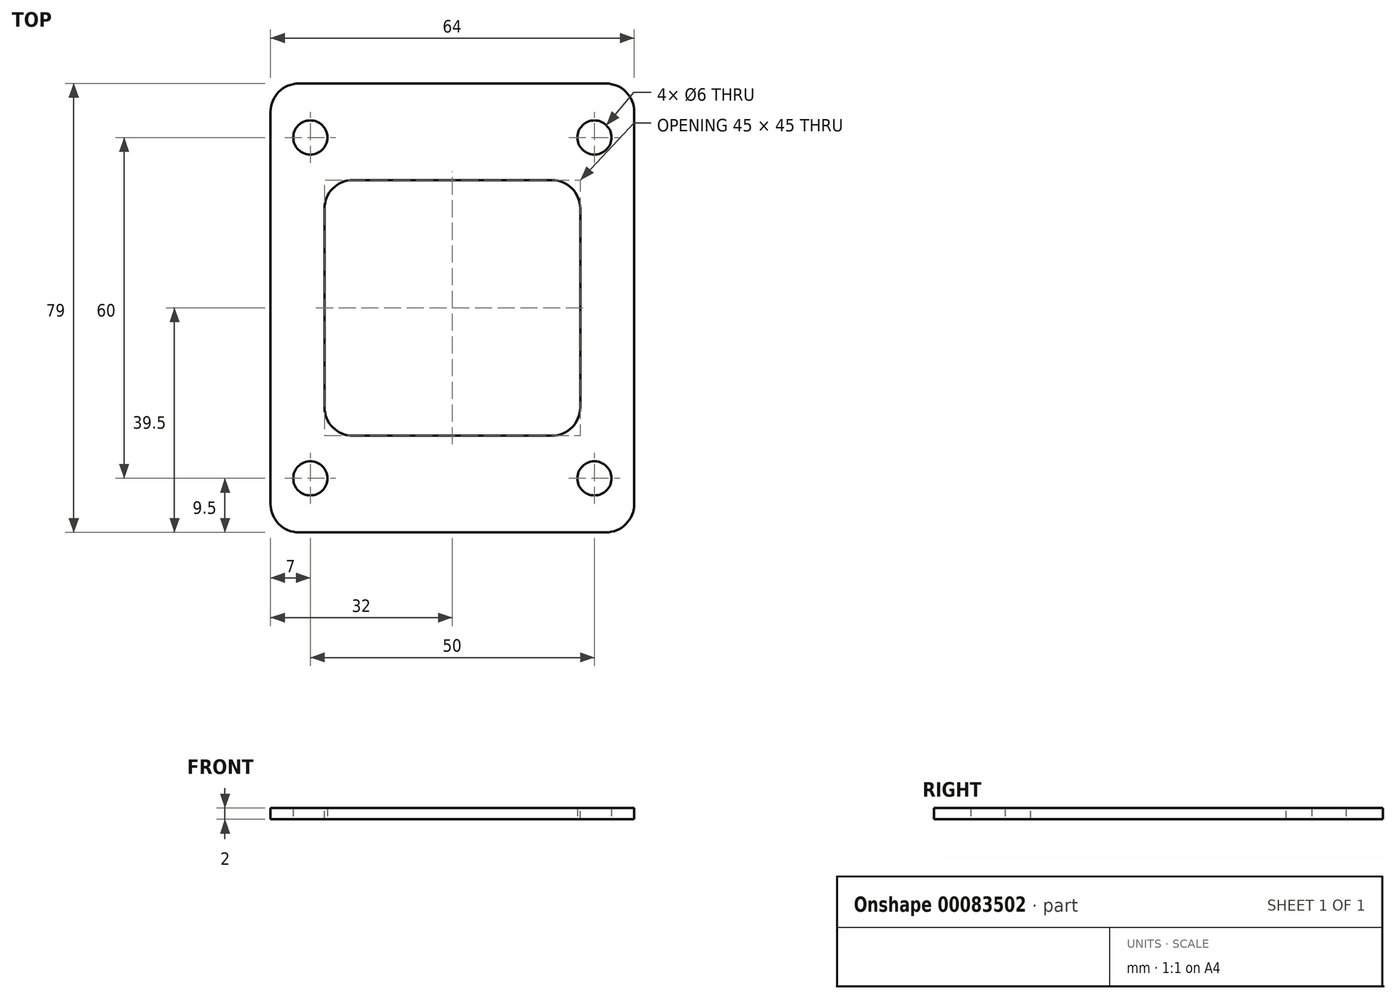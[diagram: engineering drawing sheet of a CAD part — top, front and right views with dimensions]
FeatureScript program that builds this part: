
annotation { "Feature Type Name" : "Feature", "Feature Type Description" : "" }
export const myFeature = defineFeature(function(context is Context, id is Id, definition is map)
    precondition{}
    {
        {
            var Q0;
            Q0=qCreatedBy(makeId("Top.planeOp"),FACE);
            var sketch = newSketch(context, id + "F0", { "sketchPlane" : qUnion([Q0])});
            skLineSegment(sketch, "E0.bottom", {"start": v(32, -39.5) * mm, "end": v(-32, -39.5) * mm});
            skLineSegment(sketch, "E0.top", {"start": v(32, 39.5) * mm, "end": v(-32, 39.5) * mm});
            skLineSegment(sketch, "E0.left", {"start": v(32, -39.5) * mm, "end": v(32, 39.5) * mm});
            skLineSegment(sketch, "E0.right", {"start": v(-32, -39.5) * mm, "end": v(-32, 39.5) * mm});
            skPoint(sketch, "E0.middle", {"position": v(0, 0) * mm});
            skLineSegment(sketch, "E1.bottom", {"start": v(25, -30) * mm, "end": v(-25, -30) * mm});
            skLineSegment(sketch, "E1.top", {"start": v(25, 30) * mm, "end": v(-25, 30) * mm});
            skLineSegment(sketch, "E1.left", {"start": v(25, -30) * mm, "end": v(25, 30) * mm});
            skLineSegment(sketch, "E1.right", {"start": v(-25, -30) * mm, "end": v(-25, 30) * mm});
            skSolve(sketch);
        }
        {
            var Q0;
            Q0=makeQuery(id+"F0.imprint","IMPRINT",FACE,{"disambiguationData":[TD([[makeQuery(id+"F0.imprint","IMPRINT",EDGE,{"derivedFrom":sQuery(id+"F0.wireOp",EDGE,"E1.bottom")}),-1.0]])]});
            var Q1;
            Q1=makeQuery(id+"F0.imprint","IMPRINT",FACE,{"disambiguationData":[TD([[makeQuery(id+"F0.imprint","IMPRINT",EDGE,{"derivedFrom":sQuery(id+"F0.wireOp",EDGE,"E0.bottom")}),-1.0]])]});
            extrude(context, id + "F1", {"entities" : qUnion([Q0, Q1]), "depth" : 2 * mm});
        }
        {
            var Q0;
            Q0=sQuery(id+"F0.wireOp",VERTEX,"E1.left.start");
            var Q1;
            Q1=sQuery(id+"F0.wireOp",VERTEX,"E1.right.start");
            var Q2;
            Q2=sQuery(id+"F0.wireOp",VERTEX,"E1.right.end");
            var Q3;
            Q3=sQuery(id+"F0.wireOp",VERTEX,"E1.left.end");
            var Q4;
            Q4=makeQuery(id+"F1.opExtrude","SWEPT_BODY",BODY,{"disambiguationData":[OSD([sQuery(id+"F0.wireOp",EDGE,"E0.bottom"),sQuery(id+"F0.wireOp",EDGE,"E0.top"),sQuery(id+"F0.wireOp",EDGE,"E0.left"),sQuery(id+"F0.wireOp",EDGE,"E0.right")])]});
            hole(context, id + "F2", {"style" : HoleStyle.SIMPLE, "endStyle" : HoleEndStyle.THROUGH, "oppositeDirection" : true, "holeDiameter" : 6 * mm, "locations" : qUnion([Q0, Q1, Q2, Q3]), "scope" : qUnion([Q4]), "isTappedThrough" : true});
        }
        {
            var Q0;
            Q0=makeQuery(id+"F1.opExtrude","SWEPT_EDGE",EDGE,{"disambiguationData":[OSD([sQuery(id+"F0.wireOp",EDGE,"E0.bottom"),sQuery(id+"F0.wireOp",EDGE,"E0.right")])]});
            var Q1;
            Q1=makeQuery(id+"F1.opExtrude","SWEPT_EDGE",EDGE,{"disambiguationData":[OSD([sQuery(id+"F0.wireOp",EDGE,"E0.bottom"),sQuery(id+"F0.wireOp",EDGE,"E0.left")])]});
            var Q2;
            Q2=makeQuery(id+"F1.opExtrude","SWEPT_EDGE",EDGE,{"disambiguationData":[OSD([sQuery(id+"F0.wireOp",EDGE,"E0.top"),sQuery(id+"F0.wireOp",EDGE,"E0.right")])]});
            var Q3;
            Q3=makeQuery(id+"F1.opExtrude","SWEPT_EDGE",EDGE,{"disambiguationData":[OSD([sQuery(id+"F0.wireOp",EDGE,"E0.top"),sQuery(id+"F0.wireOp",EDGE,"E0.left")])]});
            fillet(context, id + "F3", {"entities" : qUnion([Q0, Q1, Q2, Q3]), "radius" : 5 * mm, "tangentPropagation" : true, "allowEdgeOverflow" : false});
        }
        {
            var Q0;
            Q0=makeQuery(id+"F1.opExtrude","CAP_FACE",FACE,{"disambiguationData":[OSD([sQuery(id+"F0.wireOp",EDGE,"E0.bottom"),sQuery(id+"F0.wireOp",EDGE,"E0.top"),sQuery(id+"F0.wireOp",EDGE,"E0.left"),sQuery(id+"F0.wireOp",EDGE,"E0.right")])],"isStart":false});
            var sketch = newSketch(context, id + "F4", { "sketchPlane" : qUnion([Q0])});
            skLineSegment(sketch, "E2.bottom", {"start": v(22.5, 22.5) * mm, "end": v(-22.5, 22.5) * mm});
            skLineSegment(sketch, "E2.top", {"start": v(22.5, -22.5) * mm, "end": v(-22.5, -22.5) * mm});
            skLineSegment(sketch, "E2.left", {"start": v(22.5, 22.5) * mm, "end": v(22.5, -22.5) * mm});
            skLineSegment(sketch, "E2.right", {"start": v(-22.5, 22.5) * mm, "end": v(-22.5, -22.5) * mm});
            skPoint(sketch, "E2.middle", {"position": v(0, 0) * mm});
            skSolve(sketch);
        }
        {
            var Q0;
            Q0=makeQuery(id+"F4.imprint","IMPRINT",FACE,{"disambiguationData":[TD([[makeQuery(id+"F4.imprint","IMPRINT",EDGE,{"derivedFrom":sQuery(id+"F4.wireOp",EDGE,"E2.bottom")}),1.0]])]});
            extrude(context, id + "F5", {"entities" : qUnion([Q0]), "operationType" : NewBodyOperationType.REMOVE, "oppositeDirection" : true, "depth" : 25 * mm});
        }
        {
            var Q0;
            Q0=makeQuery(id+"F5.boolean.opBoolean","COPY",EDGE,{"derivedFrom":makeQuery(id+"F5.opExtrude","SWEPT_EDGE",EDGE,{"disambiguationData":[OSD([sQuery(id+"F4.wireOp",EDGE,"E2.bottom"),sQuery(id+"F4.wireOp",EDGE,"E2.right")])]})});
            var Q1;
            Q1=makeQuery(id+"F5.boolean.opBoolean","COPY",EDGE,{"derivedFrom":makeQuery(id+"F5.opExtrude","SWEPT_EDGE",EDGE,{"disambiguationData":[OSD([sQuery(id+"F4.wireOp",EDGE,"E2.bottom"),sQuery(id+"F4.wireOp",EDGE,"E2.left")])]})});
            var Q2;
            Q2=makeQuery(id+"F5.boolean.opBoolean","COPY",EDGE,{"derivedFrom":makeQuery(id+"F5.opExtrude","SWEPT_EDGE",EDGE,{"disambiguationData":[OSD([sQuery(id+"F4.wireOp",EDGE,"E2.top"),sQuery(id+"F4.wireOp",EDGE,"E2.left")])]})});
            var Q3;
            Q3=makeQuery(id+"F5.boolean.opBoolean","COPY",EDGE,{"derivedFrom":makeQuery(id+"F5.opExtrude","SWEPT_EDGE",EDGE,{"disambiguationData":[OSD([sQuery(id+"F4.wireOp",EDGE,"E2.top"),sQuery(id+"F4.wireOp",EDGE,"E2.right")])]})});
            fillet(context, id + "F6", {"entities" : qUnion([Q0, Q1, Q2, Q3]), "radius" : 5 * mm, "tangentPropagation" : true, "allowEdgeOverflow" : false});
        }
    });
